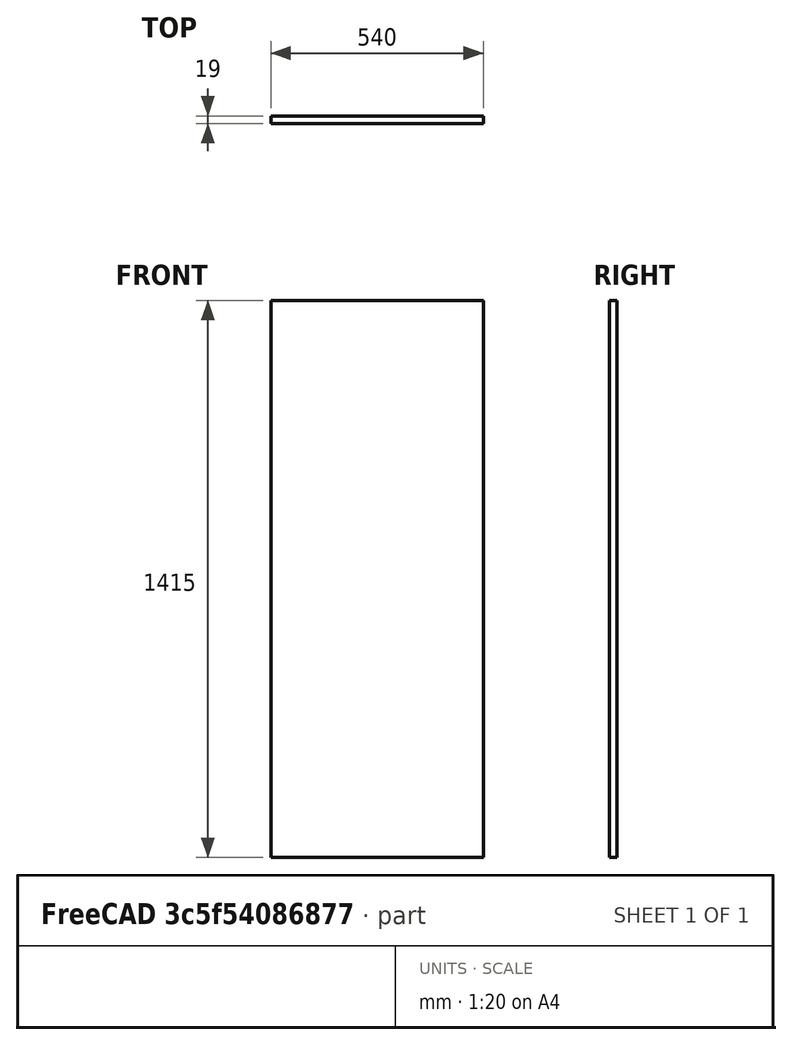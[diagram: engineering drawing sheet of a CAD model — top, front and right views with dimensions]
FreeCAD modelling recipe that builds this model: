
FCSTD DOCUMENT  (FreeCAD 1.0RUnknown)
Label: wardrobe_backplate_corpus01_jan
License: All rights reserved
LicenseURL: https://en.wikipedia.org/wiki/All_rights_reserved
objects: Sketcher::SketchObject×1, PartDesign::Pad×1, PartDesign::CoordinateSystem×1, PartDesign::Body×1
note: 7 computed .brp shape members not serialized (recipe doc carries the construction recipe); baked Part::Feature solids carry a one-line shape summary decoded from their .brp
EXTERNAL_REF file=../../mastersketch.FCStd obj=Spreadsheet

FEATURE [Sketcher::SketchObject] Sketch004
  ArcFitTolerance = 1e-06
  AttachmentSupport = -> [XZ_Plane006]
  FullyConstrained = true
  MakeInternals = false
  MapMode = 5
  Placement = pos=(0,0,0) rot=(1,0,0;1.5708rad)
  expr: Constraints[10] = mastersketch#Spreadsheet.corpus_width
  expr: Constraints[11] = mastersketch#Spreadsheet.corpus01_height
  sketch-geometry (5):
    g0: LineSegment StartX=-270 StartY=-707.5 StartZ=0 EndX=270 EndY=-707.5 EndZ=0
    g1: LineSegment StartX=270 StartY=-707.5 StartZ=0 EndX=270 EndY=707.5 EndZ=0
    g2: LineSegment StartX=270 StartY=707.5 StartZ=0 EndX=-270 EndY=707.5 EndZ=0
    g3: LineSegment StartX=-270 StartY=707.5 StartZ=0 EndX=-270 EndY=-707.5 EndZ=0
    g4: GeomPoint [constr] X=0 Y=0 Z=0
  constraints (12):
    c: Coincident(g0,g1)
    c: Coincident(g1,g2)
    c: Coincident(g2,g3)
    c: Coincident(g3,g0)
    c: Horizontal(g0)
    c: Horizontal(g2)
    c: Vertical(g1)
    c: Vertical(g3)
    c: Symmetric(g2,g0,g4)
    c: Coincident(g4,g-1)
    c: DistanceX(g0,g0) = 540
    c: DistanceY(g3,g3) = 1415
FEATURE [PartDesign::Pad] Pad004
  Direction = (0,-1,2e-16)
  Length = 19
  Length2 = 10
  Placement = pos=(0,0,0) rot=(1,0,0;1.5708rad)
  Profile = -> Sketch004
  ReferenceAxis = -> Sketch004 [N_Axis]
  Refine = true
  Suppressed = false
  Type = 0
  expr: Length = mastersketch#Spreadsheet.corpus_backplate_thickness
FEATURE [PartDesign::CoordinateSystem] LCS_bottom
  AttacherType = Attacher::AttachEngine3D
  AttachmentSupport = -> [Pad004]
  MapMode = 45
  Placement = pos=(0,0,-707.5) rot=(0.57735,0.57735,0.57735;2.0944rad)
FEATURE [PartDesign::Body] Body004  label="wardrobe_backplate_corpus01_jan"
  AllowCompound = false
  Group = -> [Sketch004,Pad004,LCS_bottom]
  Origin = -> Origin006
  Tip = -> Pad004
